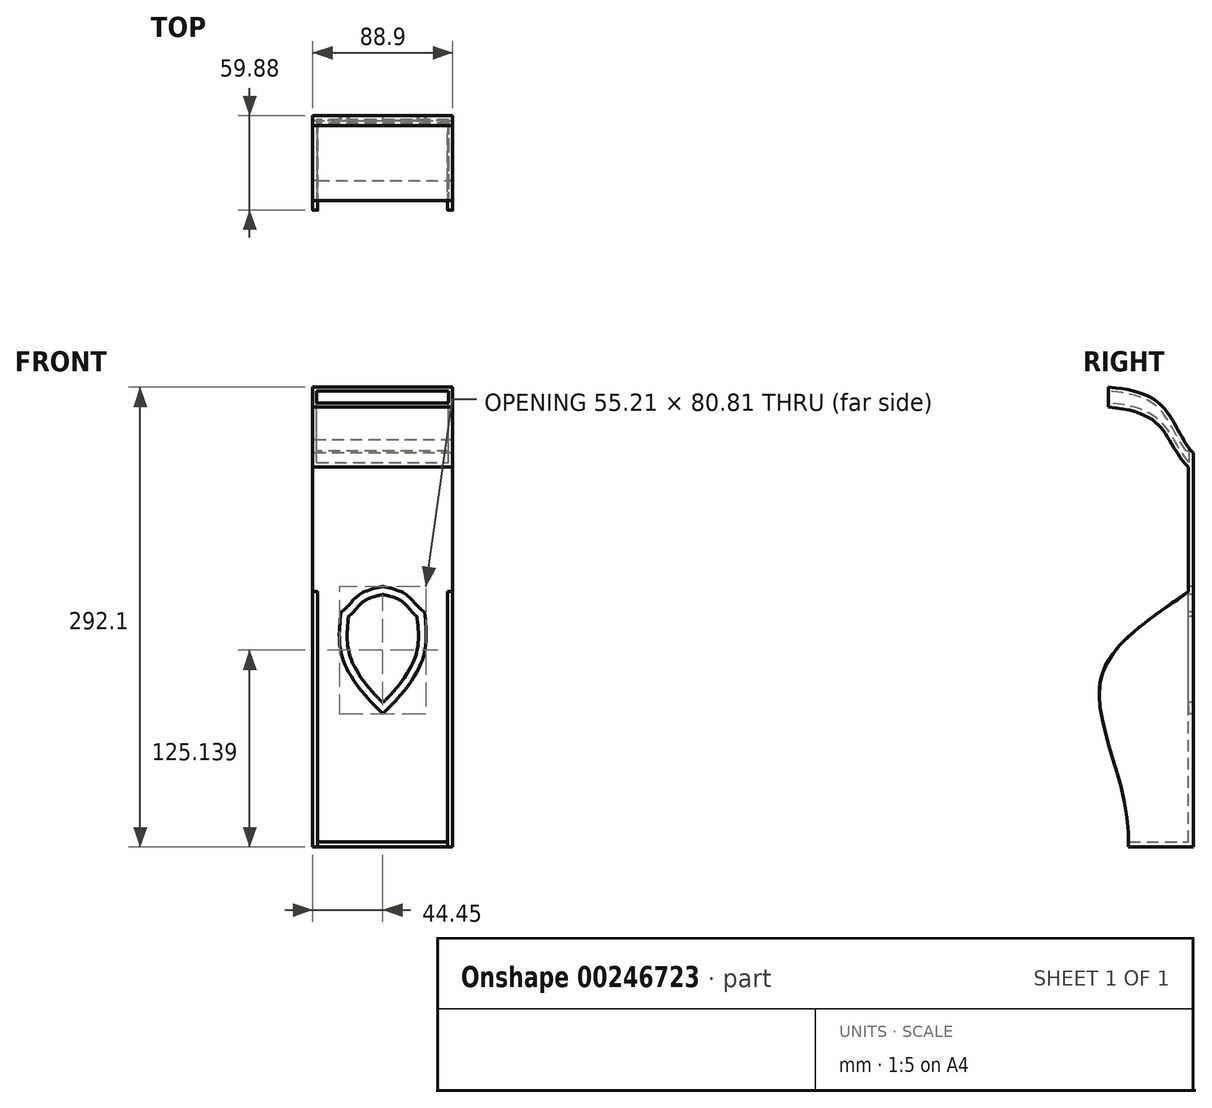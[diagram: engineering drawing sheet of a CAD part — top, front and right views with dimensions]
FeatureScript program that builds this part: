
annotation { "Feature Type Name" : "Feature", "Feature Type Description" : "" }
export const myFeature = defineFeature(function(context is Context, id is Id, definition is map)
    precondition{}
    {
        {
            var Q0;
            Q0=qCreatedBy(makeId("Front.planeOp"),FACE);
            var sketch = newSketch(context, id + "F0", { "sketchPlane" : qUnion([Q0])});
            skLineSegment(sketch, "E0.bottom", {"start": v(44.45, -127) * mm, "end": v(-44.45, -127) * mm});
            skLineSegment(sketch, "E0.top", {"start": v(44.45, 127) * mm, "end": v(-44.45, 127) * mm});
            skLineSegment(sketch, "E0.left", {"start": v(44.45, -127) * mm, "end": v(44.45, 127) * mm});
            skLineSegment(sketch, "E0.right", {"start": v(-44.45, -127) * mm, "end": v(-44.45, 127) * mm});
            skPoint(sketch, "E0.middle", {"position": v(0, 0) * mm});
            skSolve(sketch);
        }
        {
            var Q0;
            Q0 = qSketchRegion(id + "F0", true);
            extrude(context, id + "F1", {"entities" : qUnion([Q0]), "oppositeDirection" : true, "depth" : 3.17 * mm});
        }
        {
            var Q0;
            Q0=makeQuery(id+"F1.opExtrude","SWEPT_FACE",FACE,{"disambiguationData":[OSD([sQuery(id+"F0.wireOp",EDGE,"E0.left")])]});
            var sketch = newSketch(context, id + "F2", { "sketchPlane" : qUnion([Q0])});
            skFitSpline(sketch, "E1", {"points": [v(0, 35.34) * mm, v(-55.76, -20.68) * mm, v(-38.1, -127) * mm], "startDerivative": vector(-140.56, -104.08) * mm, "endDerivative": vector(-13.03, -217.65) * mm});
            skLineSegment(sketch, "E2", {"start": v(-38.1, -127) * mm, "end": v(0, -127) * mm});
            skLineSegment(sketch, "E3", {"start": v(0, -127) * mm, "end": v(0, 35.34) * mm});
            skSolve(sketch);
        }
        {
            var Q0;
            Q0 = qSketchRegion(id + "F2", true);
            extrude(context, id + "F3", {"entities" : qUnion([Q0]), "operationType" : NewBodyOperationType.ADD, "oppositeDirection" : true, "depth" : 3.17 * mm});
        }
        {
            var Q0;
            Q0=makeQuery(id+"F1.opExtrude","SWEPT_FACE",FACE,{"disambiguationData":[OSD([sQuery(id+"F0.wireOp",EDGE,"E0.right")])]});
            var sketch = newSketch(context, id + "F4", { "sketchPlane" : qUnion([Q0])});
            skLineSegment(sketch, "E4.MirrorCS", {"start": v(38.1, -127) * mm, "end": v(0, -127) * mm});
            skFitSpline(sketch, "E5.MirrorCS", {"points": [v(0, 35.34) * mm, v(55.76, -20.68) * mm, v(38.1, -127) * mm], "startDerivative": vector(140.56, -104.08) * mm, "endDerivative": vector(13.03, -217.65) * mm});
            skLineSegment(sketch, "E6.MirrorCS", {"start": v(0, -127) * mm, "end": v(0, 35.34) * mm});
            skSolve(sketch);
        }
        {
            var Q0;
            Q0 = qSketchRegion(id + "F4", true);
            extrude(context, id + "F5", {"entities" : qUnion([Q0]), "operationType" : NewBodyOperationType.ADD, "oppositeDirection" : true, "depth" : 3.17 * mm});
        }
        {
            var Q0;
            Q0=makeQuery(id+"F5.boolean.opBoolean","MERGE",FACE,{"derivedFrom":[makeQuery(id+"F3.boolean.opBoolean","MERGE",FACE,{"derivedFrom":[makeQuery(id+"F1.opExtrude","SWEPT_FACE",FACE,{"disambiguationData":[OSD([sQuery(id+"F0.wireOp",EDGE,"E0.bottom")])]}),makeQuery(id+"F3.opExtrude","SWEPT_FACE",FACE,{"disambiguationData":[OSD([sQuery(id+"F2.wireOp",EDGE,"E2")])]})]}),makeQuery(id+"F5.opExtrude","SWEPT_FACE",FACE,{"disambiguationData":[OSD([sQuery(id+"F4.wireOp",EDGE,"E4.MirrorCS")])]})]});
            var sketch = newSketch(context, id + "F6", { "sketchPlane" : qUnion([Q0])});
            skLineSegment(sketch, "E7", {"start": v(-41.28, 38.1) * mm, "end": v(41.27, 38.1) * mm});
            skLineSegment(sketch, "E8", {"start": v(41.27, 38.1) * mm, "end": v(41.27, 0) * mm});
            skLineSegment(sketch, "E9", {"start": v(41.27, 0) * mm, "end": v(-41.28, 0) * mm});
            skLineSegment(sketch, "E10", {"start": v(-41.28, 0) * mm, "end": v(-41.28, 38.1) * mm});
            skSolve(sketch);
        }
        {
            var Q0;
            Q0 = qSketchRegion(id + "F6", true);
            extrude(context, id + "F7", {"entities" : qUnion([Q0]), "operationType" : NewBodyOperationType.ADD, "oppositeDirection" : true, "depth" : 3.17 * mm});
        }
        {
            var Q0;
            Q0=makeQuery(id+"F1.opExtrude","CAP_FACE",FACE,{"disambiguationData":[OSD([sQuery(id+"F0.wireOp",EDGE,"E0.bottom"),sQuery(id+"F0.wireOp",EDGE,"E0.top"),sQuery(id+"F0.wireOp",EDGE,"E0.left"),sQuery(id+"F0.wireOp",EDGE,"E0.right")])],"isStart":true});
            var sketch = newSketch(context, id + "F8", { "sketchPlane" : qUnion([Q0])});
            skLineSegment(sketch, "E11.bottom", {"start": v(-44.45, 127) * mm, "end": v(44.45, 127) * mm});
            skLineSegment(sketch, "E11.top", {"start": v(-44.45, 114.3) * mm, "end": v(44.45, 114.3) * mm});
            skLineSegment(sketch, "E11.left", {"start": v(-44.45, 127) * mm, "end": v(-44.45, 114.3) * mm});
            skLineSegment(sketch, "E11.right", {"start": v(44.45, 127) * mm, "end": v(44.45, 114.3) * mm});
            skSolve(sketch);
        }
        {
            var Q0;
            Q0=qCreatedBy(makeId("Front.planeOp"),FACE);
            cPlane(context, id + "F9", {"entities" : qUnion([Q0]), "cplaneType" : CPlaneType.OFFSET, "offset" : 50.8 * mm, "width" : 152.4 * mm, "height" : 152.4 * mm});
        }
        {
            var Q0;
            Q0=qCreatedBy(id+"F9.planeOp",FACE);
            var sketch = newSketch(context, id + "F10", { "sketchPlane" : qUnion([Q0])});
            skLineSegment(sketch, "E12.bottom", {"start": v(-44.45, 165.1) * mm, "end": v(44.45, 165.1) * mm});
            skLineSegment(sketch, "E12.top", {"start": v(-44.45, 152.4) * mm, "end": v(44.45, 152.4) * mm});
            skLineSegment(sketch, "E12.left", {"start": v(-44.45, 165.1) * mm, "end": v(-44.45, 152.4) * mm});
            skLineSegment(sketch, "E12.right", {"start": v(44.45, 165.1) * mm, "end": v(44.45, 152.4) * mm});
            skLineSegment(sketch, "E13", {"start": v(-44.45, 83.9) * mm, "end": v(-44.45, 115.08) * mm, "construction": true});
            skLineSegment(sketch, "E14", {"start": v(44.45, 110.88) * mm, "end": v(44.45, 89.41) * mm, "construction": true});
            skSolve(sketch);
        }
        {
            var Q0;
            Q0=makeQuery(id+"F5.boolean.opBoolean","MERGE",FACE,{"derivedFrom":[makeQuery(id+"F1.opExtrude","SWEPT_FACE",FACE,{"disambiguationData":[OSD([sQuery(id+"F0.wireOp",EDGE,"E0.right")])]}),makeQuery(id+"F5.opExtrude","CAP_FACE",FACE,{"disambiguationData":[OSD([sQuery(id+"F4.wireOp",EDGE,"E4.MirrorCS"),sQuery(id+"F4.wireOp",EDGE,"E5.MirrorCS"),sQuery(id+"F4.wireOp",EDGE,"E6.MirrorCS")])],"isStart":true})]});
            var sketch = newSketch(context, id + "F11", { "sketchPlane" : qUnion([Q0])});
            skFitSpline(sketch, "E15", {"points": [v(0, 114.3) * mm, v(50.8, 152.4) * mm], "startDerivative": vector(47.99, 48.71) * mm, "endDerivative": vector(117.66, 8.05) * mm});
            skFitSpline(sketch, "E16", {"points": [v(0, 127) * mm, v(50.8, 165.1) * mm], "startDerivative": vector(38.93, 54.68) * mm, "endDerivative": vector(117.66, 8.05) * mm});
            skSolve(sketch);
        }
        {
            var Q0;
            Q0=makeQuery(id+"F3.boolean.opBoolean","MERGE",FACE,{"derivedFrom":[makeQuery(id+"F1.opExtrude","SWEPT_FACE",FACE,{"disambiguationData":[OSD([sQuery(id+"F0.wireOp",EDGE,"E0.left")])]}),makeQuery(id+"F3.opExtrude","CAP_FACE",FACE,{"disambiguationData":[OSD([sQuery(id+"F2.wireOp",EDGE,"E1"),sQuery(id+"F2.wireOp",EDGE,"E2"),sQuery(id+"F2.wireOp",EDGE,"E3")])],"isStart":true})]});
            var sketch = newSketch(context, id + "F12", { "sketchPlane" : qUnion([Q0])});
            skFitSpline(sketch, "E17.MirrorCS", {"points": [v(0, 127) * mm, v(-50.8, 165.1) * mm], "startDerivative": vector(-38.93, 54.68) * mm, "endDerivative": vector(-117.66, 8.05) * mm});
            skFitSpline(sketch, "E18.MirrorCS", {"points": [v(0, 114.3) * mm, v(-50.8, 152.4) * mm], "startDerivative": vector(-47.99, 48.71) * mm, "endDerivative": vector(-117.66, 8.05) * mm});
            skSolve(sketch);
        }
        {
            var Q1;
            Q1=makeQuery(id+"F8.imprint","IMPRINT",FACE,{"disambiguationData":[TD([[makeQuery(id+"F8.imprint","IMPRINT",EDGE,{"derivedFrom":sQuery(id+"F8.wireOp",EDGE,"E11.bottom")}),1.0]])]});
            var Q2;
            Q2=makeQuery(id+"F10.imprint","IMPRINT",FACE,{"disambiguationData":[TD([[makeQuery(id+"F10.imprint","IMPRINT",EDGE,{"derivedFrom":sQuery(id+"F10.wireOp",EDGE,"E12.bottom")}),-1.0]])]});
            var Q3;
            Q3=sQuery(id+"F11.wireOp",EDGE,"E16");
            var Q4;
            Q4=sQuery(id+"F11.wireOp",EDGE,"E15");
            var Q5;
            Q5=sQuery(id+"F12.wireOp",EDGE,"E17.MirrorCS");
            var Q6;
            Q6=sQuery(id+"F12.wireOp",EDGE,"E18.MirrorCS");
            loft(context, id + "F13", {"operationType" : NewBodyOperationType.ADD, "addGuides" : true, "sheetProfilesArray" : [{ "sheetProfileEntities" : qUnion([Q1]) }, { "sheetProfileEntities" : qUnion([Q2]) }], "guidesArray" : [{ "guideEntities" : qUnion([Q3]), "guideDerivativeType" : LoftGuideDerivativeType.DEFAULT, "guideDerivativeMagnitude" : 1 }, { "guideEntities" : qUnion([Q4]), "guideDerivativeType" : LoftGuideDerivativeType.DEFAULT, "guideDerivativeMagnitude" : 1 }, { "guideEntities" : qUnion([Q5]), "guideDerivativeType" : LoftGuideDerivativeType.DEFAULT, "guideDerivativeMagnitude" : 1 }, { "guideEntities" : qUnion([Q6]), "guideDerivativeType" : LoftGuideDerivativeType.DEFAULT, "guideDerivativeMagnitude" : 1 }]});
        }
        {
            var Q0;
            Q0=makeQuery(id+"F13.opLoft","CAP_FACE",FACE,{"disambiguationData":[OSD([makeQuery(id+"F10.imprint","IMPRINT",FACE,{"disambiguationData":[TD([[makeQuery(id+"F10.imprint","IMPRINT",EDGE,{"derivedFrom":sQuery(id+"F10.wireOp",EDGE,"E12.bottom")}),-1.0]])]})])],"isStart":true});
            var Q1;
            Q1=makeQuery(id+"F1.opExtrude","SWEPT_BODY",BODY,{"disambiguationData":[OSD([sQuery(id+"F0.wireOp",EDGE,"E0.bottom"),sQuery(id+"F0.wireOp",EDGE,"E0.top"),sQuery(id+"F0.wireOp",EDGE,"E0.left"),sQuery(id+"F0.wireOp",EDGE,"E0.right")])]});
            shell(context, id + "F14", {"entities" : qUnion([Q0]), "parts" : qUnion([Q1]), "thickness" : 2.54 * mm});
        }
        {
            var Q0;
            Q0=makeQuery(id+"F1.opExtrude","CAP_FACE",FACE,{"disambiguationData":[OSD([sQuery(id+"F0.wireOp",EDGE,"E0.bottom"),sQuery(id+"F0.wireOp",EDGE,"E0.top"),sQuery(id+"F0.wireOp",EDGE,"E0.left"),sQuery(id+"F0.wireOp",EDGE,"E0.right")])],"isStart":true});
            var sketch = newSketch(context, id + "F15", { "sketchPlane" : qUnion([Q0])});
            skLineSegment(sketch, "E19", {"start": v(0, -55.93) * mm, "end": v(0, 133.02) * mm, "construction": true});
            skFitSpline(sketch, "E20", {"points": [v(0, -42.27) * mm, v(-26.56, 22.4) * mm], "startDerivative": vector(-94.3, 90.59) * mm, "endDerivative": vector(5.6, 60.7) * mm});
            skFitSpline(sketch, "E21", {"points": [v(-26.56, 22.4) * mm, v(0, 38.54) * mm], "startDerivative": vector(26.54, 16.11) * mm, "endDerivative": vector(61.85, 11.63) * mm});
            skFitSpline(sketch, "E22.MirrorCS", {"points": [v(0, -42.27) * mm, v(26.56, 22.4) * mm], "startDerivative": vector(94.3, 90.59) * mm, "endDerivative": vector(-5.6, 60.7) * mm});
            skFitSpline(sketch, "E23.MirrorCS", {"points": [v(26.56, 22.4) * mm, v(0, 38.54) * mm], "startDerivative": vector(-26.54, 16.11) * mm, "endDerivative": vector(-61.85, 11.63) * mm});
            skFitSpline(sketch, "E24.0", {"points": [v(23.93, 18.05) * mm, v(23.24, 18.47) * mm, v(21.97, 19.32) * mm, v(20.33, 20.66) * mm, v(18.93, 22) * mm, v(17.75, 23.29) * mm, v(16.73, 24.5) * mm, v(15.82, 25.57) * mm, v(14.99, 26.54) * mm, v(14.16, 27.4) * mm, v(13.28, 28.2) * mm, v(12.27, 28.97) * mm, v(11.05, 29.74) * mm, v(9.03, 30.79) * mm, v(5.57, 32.1) * mm, v(1.5, 33.1) * mm, v(-0.94, 33.55) * mm]});
            skFitSpline(sketch, "E24.1", {"points": [v(-3.52, -38.6) * mm, v(0.32, -34.91) * mm, v(6.9, -28.06) * mm, v(13.91, -19.17) * mm, v(18.48, -11.45) * mm, v(21.13, -4.66) * mm, v(22.39, 1.62) * mm, v(22.65, 7.88) * mm, v(22.24, 14.52) * mm, v(21.74, 19.37) * mm, v(21.5, 21.93) * mm]});
            skFitSpline(sketch, "E24.2", {"points": [v(3.52, -38.6) * mm, v(-0.32, -34.91) * mm, v(-6.9, -28.06) * mm, v(-13.91, -19.17) * mm, v(-18.48, -11.45) * mm, v(-21.13, -4.66) * mm, v(-22.39, 1.62) * mm, v(-22.65, 7.88) * mm, v(-22.24, 14.52) * mm, v(-21.74, 19.37) * mm, v(-21.5, 21.93) * mm]});
            skFitSpline(sketch, "E24.3", {"points": [v(-23.93, 18.05) * mm, v(-23.24, 18.47) * mm, v(-21.97, 19.32) * mm, v(-20.33, 20.66) * mm, v(-18.93, 22) * mm, v(-17.75, 23.29) * mm, v(-16.73, 24.5) * mm, v(-15.82, 25.57) * mm, v(-14.99, 26.54) * mm, v(-14.16, 27.4) * mm, v(-13.28, 28.2) * mm, v(-12.27, 28.97) * mm, v(-11.05, 29.74) * mm, v(-9.03, 30.79) * mm, v(-5.57, 32.1) * mm, v(-1.5, 33.1) * mm, v(0.94, 33.55) * mm]});
            skLineSegment(sketch, "E25", {"start": v(4.83, 37.48) * mm, "end": v(4.83, 32.21) * mm});
            skLineSegment(sketch, "E26.MirrorCS", {"start": v(-4.83, 37.48) * mm, "end": v(-4.83, 32.21) * mm});
            skLineSegment(sketch, "E27.trimOffspring", {"start": v(4.83, -30.08) * mm, "end": v(4.83, -37.48) * mm});
            skLineSegment(sketch, "E28.trimOffspring", {"start": v(-4.83, -30.08) * mm, "end": v(-4.83, -37.48) * mm});
            skText(sketch, "E29", { "text": "OD", "fontName": "AllertaStencil-Regular.ttf"});
            skText(sketch, "E30", { "text": "W", "fontName": "AllertaStencil-Regular.ttf"});
            skLineSegment(sketch, "E31", {"start": v(-56.3, 0) * mm, "end": v(83.4, 0) * mm, "construction": true});
            const initialGuessF15  = {"E29": [-0.01742, 0.00327, 1, 0, 0.01682], "E30": [-0.01143, -0.01766, 1, 0, 0.01545]};
            skSetInitialGuess(sketch, initialGuessF15);
            skSolve(sketch);
        }
        {
            var Q0;
            Q0 = qSketchRegion(id + "F15", true);
            extrude(context, id + "F16", {"entities" : qUnion([Q0]), "operationType" : NewBodyOperationType.REMOVE, "oppositeDirection" : true, "depth" : 25.4 * mm});
        }
        {
            var Q0;
            Q0=makeQuery(id+"F13.boolean.opBoolean","MERGE",FACE,{"derivedFrom":[makeQuery(id+"F5.boolean.opBoolean","MERGE",FACE,{"derivedFrom":[makeQuery(id+"F1.opExtrude","SWEPT_FACE",FACE,{"disambiguationData":[OSD([sQuery(id+"F0.wireOp",EDGE,"E0.right")])]}),makeQuery(id+"F5.opExtrude","CAP_FACE",FACE,{"disambiguationData":[OSD([sQuery(id+"F4.wireOp",EDGE,"E4.MirrorCS"),sQuery(id+"F4.wireOp",EDGE,"E5.MirrorCS"),sQuery(id+"F4.wireOp",EDGE,"E6.MirrorCS")])],"isStart":true})]}),makeQuery(id+"F13.opLoft","SWEPT_FACE",FACE,{"disambiguationData":[OSD([sQuery(id+"F8.wireOp",EDGE,"E11.top"),sQuery(id+"F8.wireOp",EDGE,"E11.left"),sQuery(id+"F10.wireOp",EDGE,"E12.top"),sQuery(id+"F10.wireOp",EDGE,"E12.left"),sQuery(id+"F11.wireOp",EDGE,"E15"),sQuery(id+"F11.wireOp",EDGE,"E16")])]})]});
            var sketch = newSketch(context, id + "F17", { "sketchPlane" : qUnion([Q0])});
            skFitSpline(sketch, "E32", {"points": [v(-14.55, 116.44) * mm, v(3, 131.57) * mm], "startDerivative": vector(22.77, 8.23) * mm, "endDerivative": vector(11.25, 21.67) * mm});
            skLineSegment(sketch, "E33", {"start": v(-14.55, 116.44) * mm, "end": v(-14.55, 131.57) * mm});
            skLineSegment(sketch, "E34", {"start": v(-14.55, 131.57) * mm, "end": v(3, 131.57) * mm});
            skSolve(sketch);
        }
        {
            var Q0;
            Q0 = qSketchRegion(id + "F17", true);
            var Q1;
            Q1=makeQuery(id+"F13.boolean.opBoolean","MERGE",FACE,{"derivedFrom":[makeQuery(id+"F3.boolean.opBoolean","MERGE",FACE,{"derivedFrom":[makeQuery(id+"F1.opExtrude","SWEPT_FACE",FACE,{"disambiguationData":[OSD([sQuery(id+"F0.wireOp",EDGE,"E0.left")])]}),makeQuery(id+"F3.opExtrude","CAP_FACE",FACE,{"disambiguationData":[OSD([sQuery(id+"F2.wireOp",EDGE,"E1"),sQuery(id+"F2.wireOp",EDGE,"E2"),sQuery(id+"F2.wireOp",EDGE,"E3")])],"isStart":true})]}),makeQuery(id+"F13.opLoft","SWEPT_FACE",FACE,{"disambiguationData":[OSD([sQuery(id+"F8.wireOp",EDGE,"E11.right"),sQuery(id+"F10.wireOp",EDGE,"E12.right"),sQuery(id+"F12.wireOp",EDGE,"E17.MirrorCS"),sQuery(id+"F12.wireOp",EDGE,"E18.MirrorCS")])]})]});
            extrude(context, id + "F18", {"entities" : qUnion([Q0]), "operationType" : NewBodyOperationType.REMOVE, "endBound" : BoundingType.UP_TO_SURFACE, "oppositeDirection" : true, "endBoundEntityFace" : qUnion([Q1]), "depth" : 25.4 * mm});
        }
    });
